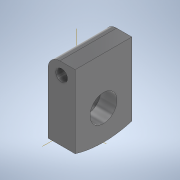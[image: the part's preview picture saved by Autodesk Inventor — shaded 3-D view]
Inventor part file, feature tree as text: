
AUTODESK INVENTOR PART (.ipt)
format: ipt  version: 2021.1 (Build 251245000, 245)  size: 129,536 bytes
history: native  units: in
note: dims shown in document units (in); Inventor stores cm internally (conversion verified against a paired STEP export)
features: sketch x3, extrude x2, fillet x1, hole x1
ambient origin geometry x8: Origin, YZ Plane, XZ Plane, XY Plane, X Axis, Y Axis, Z Axis, Center Point
bodies: Solid1 (feature_tree)
feature tree (7):
  extrude  "Extrusion1"  Depth=2.4803in
  fillet  "Fillet1"  [1 undecoded]
  extrude  "Extrusion2"  Depth=0.5118in
  hole  "Hole1"  [1 undecoded]
  sketch  "Sketch1"  dims[d0=4.252in d1=2.4803in d2=0.0in]
  sketch  "Sketch2"  dims[d3=1.1811in d4=0.0in d5=0.5118in]
  sketch  "Sketch3"  dims[d7=0.5118in d8=0.5906in d9=0.5118in d10=0.0in d11=0.0in d12=1.2992in d13=1.1811in d14=0.2362in d15=1.6535in d16=0.4724in d17=90.0deg d18=0.315in d19=0.8108in]
note: 2 required parameter values undecoded (feature->parameter linkage not recoverable at this tier; creation-order binding heuristic only, values carry confidence <= 0.55)
